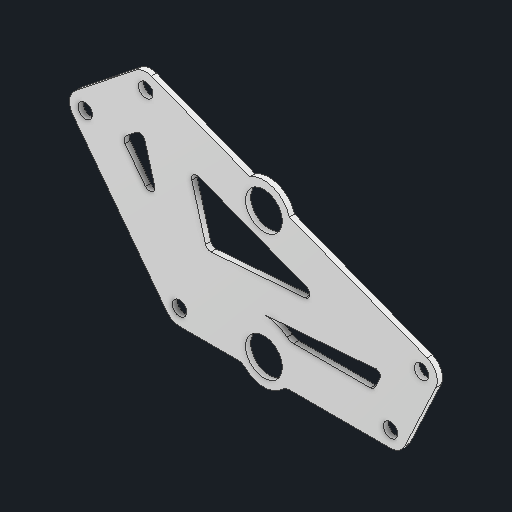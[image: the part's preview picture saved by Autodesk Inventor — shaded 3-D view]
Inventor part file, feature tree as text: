
AUTODESK INVENTOR PART (.ipt)
format: ipt  version: 2025 (Build 290162000, 162)  size: 183,808 bytes
history: native  units: in
note: dims shown in document units (in); Inventor stores cm internally (conversion verified against a paired STEP export)
features: other x3, extrude x1, sketch x1
ambient origin geometry x8: Origin, YZ Plane, XZ Plane, XY Plane, X Axis, Y Axis, Z Axis, Center Point
bodies: Solid1 (feature_tree)
feature tree (5):
  other  "Blocks"
  extrude  "Extrusion1"  Depth=0.375in
  sketch  "Sketch1"  dims[d0=0.375in d1=0.375in d2=0.375in d3=0.375in d4=0.375in d5=0.5in d7=0.375in d8=0.0625in d9=0.0625in d10=0.0625in d11=0.0in d13=0.4375in d14=0.5in d15=0.625in d16=0.125in d18=0.4375in d19=0.625in d20=0.5in d21=0.5in d22=0.5in d23=0.5in]
  other  "main"
  other  "main:1"
